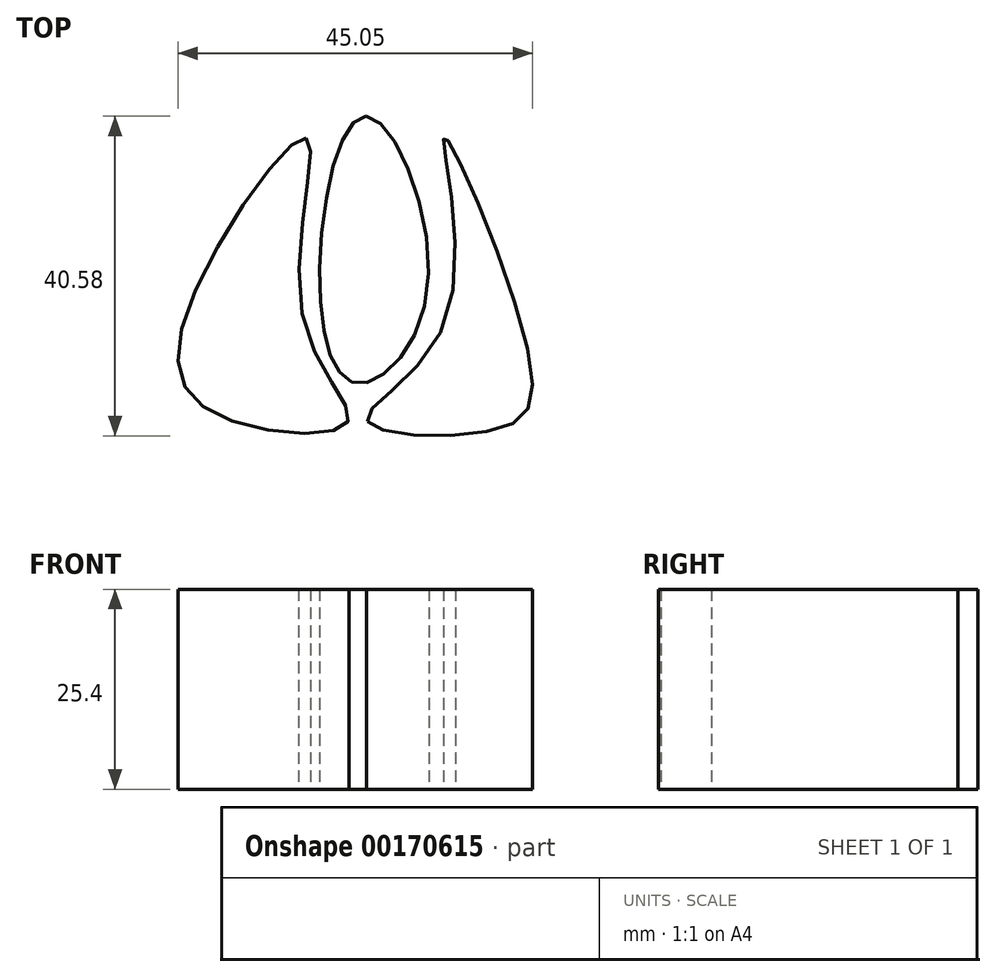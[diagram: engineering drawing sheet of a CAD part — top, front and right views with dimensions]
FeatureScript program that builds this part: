
annotation { "Feature Type Name" : "Feature", "Feature Type Description" : "" }
export const myFeature = defineFeature(function(context is Context, id is Id, definition is map)
    precondition{}
    {
        {
            var Q0;
            Q0=qCreatedBy(makeId("Top.planeOp"),FACE);
            var sketch = newSketch(context, id + "F0", { "sketchPlane" : qUnion([Q0])});
            skFitSpline(sketch, "E0", {"points": [v(-31.02, 39.91) * mm, v(-46.13, 17.89) * mm, v(-42.68, 4.93) * mm, v(-25.83, 3.63) * mm, v(-31.45, 17.02) * mm, v(-31.02, 39.91) * mm]});
            skFitSpline(sketch, "E1", {"points": [v(-23.25, 3.9) * mm, v(-6.82, 2.89) * mm, v(-2.5, 11.1) * mm, v(-13.45, 40.07) * mm, v(-13.3, 16.72) * mm, v(-23.25, 3.9) * mm]});
            skFitSpline(sketch, "E2", {"points": [v(-23.4, 42.66) * mm, v(-29.3, 22.77) * mm, v(-24.7, 8.8) * mm, v(-15.61, 20.47) * mm, v(-23.4, 42.66) * mm]});
            skSolve(sketch);
        }
        {
            var Q0;
            Q0 = qSketchRegion(id + "F0", true);
            extrude(context, id + "F1", {"entities" : qUnion([Q0]), "depth" : 25.4 * mm});
        }
    });
